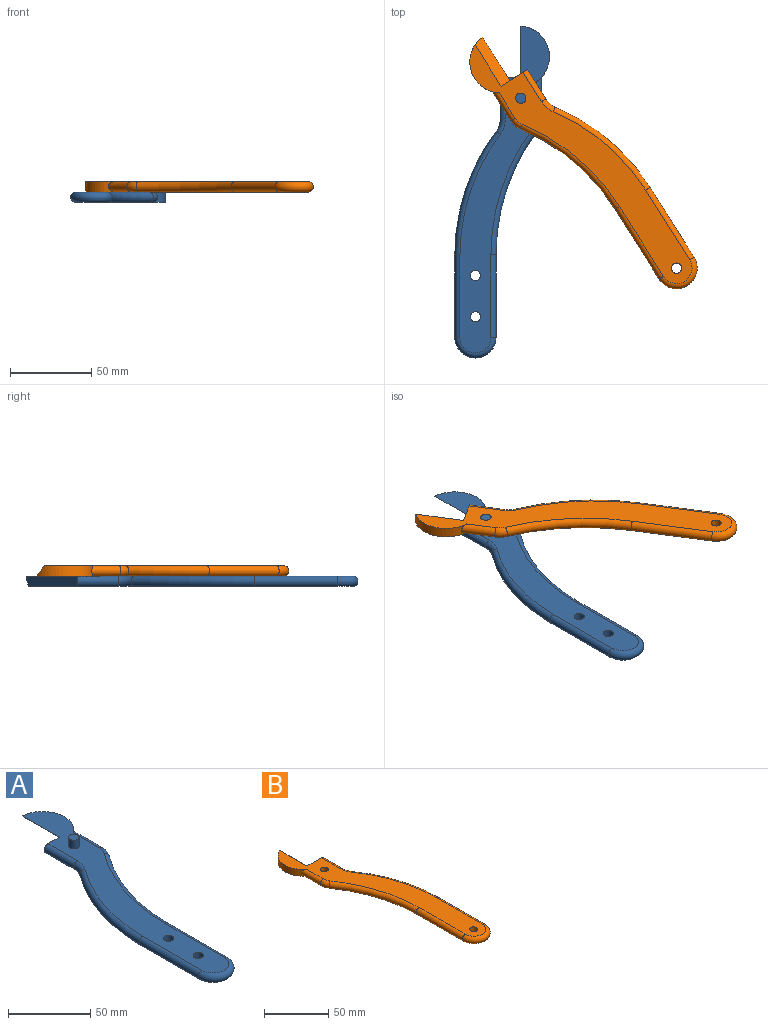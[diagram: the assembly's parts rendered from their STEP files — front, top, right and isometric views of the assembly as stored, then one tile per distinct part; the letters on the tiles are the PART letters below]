
ASSEMBLY  parts=2 mates=1
PART A: 18 faces, bbox 68.7x205.5x12.7 mm
  f0: cylinder r=19.05mm len=34.57mm, axis (0,0,-1), area 255.1mm2, adj f2,f3,f4,f15
  f1: plane 19.05x6.35mm, normal (0,1,0), area 96.5mm2, adj f2,f3,f4,f7
  f2: plane 201.3x55.07mm, normal (0,0,1), area 3524.4mm2, adj f0,f1,f4,f5,f7,f8,f9,f10
  f3: plane 199.68x55.07mm, normal (0,0,-1), area 3358.3mm2, adj f0,f1,f4,f7,f8,f9,f10,f11
  f4: plane 31.75x6.35mm, normal (-0.71,0,-0.71), area 279.6mm2, adj f0,f1,f2,f3
  f5: cylinder r=3.17mm len=6.35mm, axis (0,0,-1), area 126.7mm2, adj f2,f6
  f6: plane 6.35x6.35mm, normal (0,0,1), area 31.7mm2, adj f5
  f7: cylinder r=3.17mm len=25.4mm, axis (0,-1,0), area 253.4mm2, adj f1,f2,f3,f8
  f8: torus R=15.88mm, axis (0,0,1), area 88.9mm2, adj f2,f3,f7,f9
  f9: torus R=123.83mm, axis (0,0,1), area 807.8mm2, adj f2,f3,f8,f10
  f10: cylinder r=3.17mm len=50.8mm, axis (0,-1,0), area 506.7mm2, adj f2,f3,f9,f11
  f11: torus R=9.53mm, axis (0,0,1), area 361.8mm2, adj f2,f3,f10,f12
  f12: cylinder r=3.17mm len=50.8mm, axis (0,1,0), area 506.7mm2, adj f2,f3,f11,f13
  f13: torus R=130.18mm, axis (0,0,1), area 822.6mm2, adj f2,f3,f12,f14
  f14: torus R=9.53mm, axis (0,0,1), area 74.1mm2, adj f2,f3,f13,f15
  f15: cylinder r=3.17mm len=25.4mm, axis (0,1,0), area 242.3mm2, adj f0,f2,f3,f14
  f16: cylinder r=3.17mm len=6.35mm, axis (0,0,1), area 126.7mm2, adj f2,f3
  f17: cylinder r=3.17mm len=6.35mm, axis (0,0,1), area 126.7mm2, adj f2,f3
PART B: 16 faces, bbox 66.2x197.9x6.4 mm
  f0: cylinder r=19.05mm len=34.57mm, axis (0,0,-1), area 255.1mm2, adj f3,f4,f5,f6
  f1: cylinder r=3.17mm len=6.35mm, axis (0,0,-1), area 126.7mm2, adj f3,f4
  f2: plane 19.05x6.35mm, normal (0,1,0), area 96.5mm2, adj f3,f4,f5,f14
  f3: plane 192.06x52.53mm, normal (0,0,1), area 3218.4mm2, adj f0,f1,f2,f5,f6,f7,f8,f9
  f4: plane 193.68x52.53mm, normal (0,0,-1), area 3416.2mm2, adj f0,f1,f2,f5,f6,f7,f8,f9
  f5: plane 31.75x6.35mm, normal (0.71,0,0.71), area 279.6mm2, adj f0,f2,f3,f4
  f6: cylinder r=3.17mm len=21.28mm, axis (0,1,0), area 201.2mm2, adj f0,f3,f4,f7
  f7: torus R=9.53mm, axis (0,0,1), area 70.5mm2, adj f3,f4,f6,f8
  f8: torus R=130.18mm, axis (0,0,1), area 783mm2, adj f3,f4,f7,f9
  f9: cylinder r=3.17mm len=50.8mm, axis (0,1,0), area 506.7mm2, adj f3,f4,f8,f10
  f10: torus R=9.53mm, axis (0,0,1), area 361.8mm2, adj f3,f4,f9,f11
  f11: cylinder r=3.17mm len=50.8mm, axis (0,-1,0), area 506.7mm2, adj f3,f4,f10,f12
  f12: torus R=123.83mm, axis (0,0,1), area 768.9mm2, adj f3,f4,f11,f13
  f13: torus R=15.88mm, axis (0,0,1), area 84.6mm2, adj f3,f4,f12,f14
  f14: cylinder r=3.17mm len=21.28mm, axis (0,-1,0), area 212.2mm2, adj f2,f3,f4,f13
  f15: cylinder r=3.17mm len=6.35mm, axis (0,0,1), area 126.7mm2, adj f3,f4
PLACE A t=(-29.7,-14.4,-2.9)mm fixed
PLACE B rot(axis=(0,0,1),32.2deg) t=(94.3,-28.36,3.45)mm
MATE cylindrical B.f1 <-> A.f5  axis (0,0,1) through (0.42,53.68,9.8)mm
